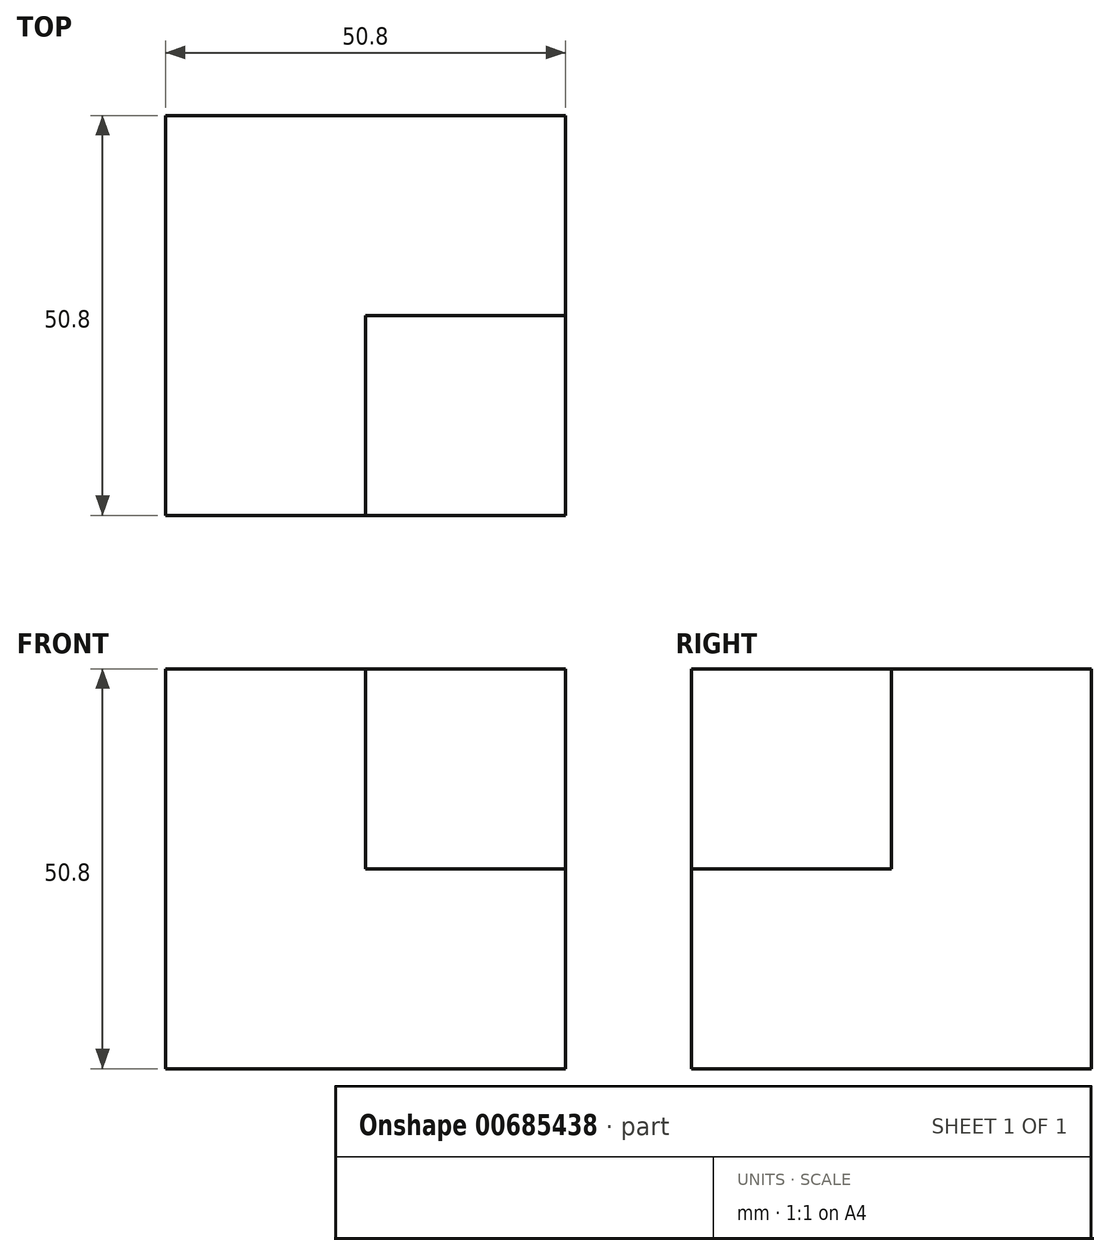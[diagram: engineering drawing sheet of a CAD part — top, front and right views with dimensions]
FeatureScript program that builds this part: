
annotation { "Feature Type Name" : "Feature", "Feature Type Description" : "" }
export const myFeature = defineFeature(function(context is Context, id is Id, definition is map)
    precondition{}
    {
        {
            var Q0;
            Q0=qCreatedBy(makeId("Front.planeOp"),FACE);
            var sketch = newSketch(context, id + "F0", { "sketchPlane" : qUnion([Q0])});
            skLineSegment(sketch, "E0.bottom", {"start": v(-69.88, 50.8) * mm, "end": v(-19.08, 50.8) * mm});
            skLineSegment(sketch, "E0.top", {"start": v(-69.88, 0) * mm, "end": v(-19.08, 0) * mm});
            skLineSegment(sketch, "E0.left", {"start": v(-69.88, 50.8) * mm, "end": v(-69.88, 0) * mm});
            skLineSegment(sketch, "E0.right", {"start": v(-19.08, 50.8) * mm, "end": v(-19.08, 0) * mm});
            skSolve(sketch);
        }
        {
            var Q0;
            Q0 = qSketchRegion(id + "F0", true);
            var Q1;
            Q1 = qSketchRegion(id + "FPoq8R0vb9N8okm_1", true);
            extrude(context, id + "F1", {"entities" : qUnion([Q0, Q1]), "depth" : 50.8 * mm, "offsetDistance" : 25.4 * mm});
        }
        {
            var Q0;
            Q0=makeQuery(id+"F1.opExtrude","CAP_FACE",FACE,{"disambiguationData":[OSD([sQuery(id+"F0.wireOp",EDGE,"E0.bottom"),sQuery(id+"F0.wireOp",EDGE,"E0.top"),sQuery(id+"F0.wireOp",EDGE,"E0.left"),sQuery(id+"F0.wireOp",EDGE,"E0.right")])],"isStart":false});
            var sketch = newSketch(context, id + "F2", { "sketchPlane" : qUnion([Q0])});
            skLineSegment(sketch, "E1.bottom", {"start": v(-19.08, 50.8) * mm, "end": v(-44.48, 50.8) * mm});
            skLineSegment(sketch, "E1.top", {"start": v(-19.08, 25.4) * mm, "end": v(-44.48, 25.4) * mm});
            skLineSegment(sketch, "E1.left", {"start": v(-19.08, 50.8) * mm, "end": v(-19.08, 25.4) * mm});
            skLineSegment(sketch, "E1.right", {"start": v(-44.48, 50.8) * mm, "end": v(-44.48, 25.4) * mm});
            skSolve(sketch);
        }
        {
            var Q0;
            Q0 = qSketchRegion(id + "F2", true);
            extrude(context, id + "F3", {"entities" : qUnion([Q0]), "operationType" : NewBodyOperationType.REMOVE, "oppositeDirection" : true, "depth" : 25.4 * mm, "offsetDistance" : 25.4 * mm});
        }
    });
